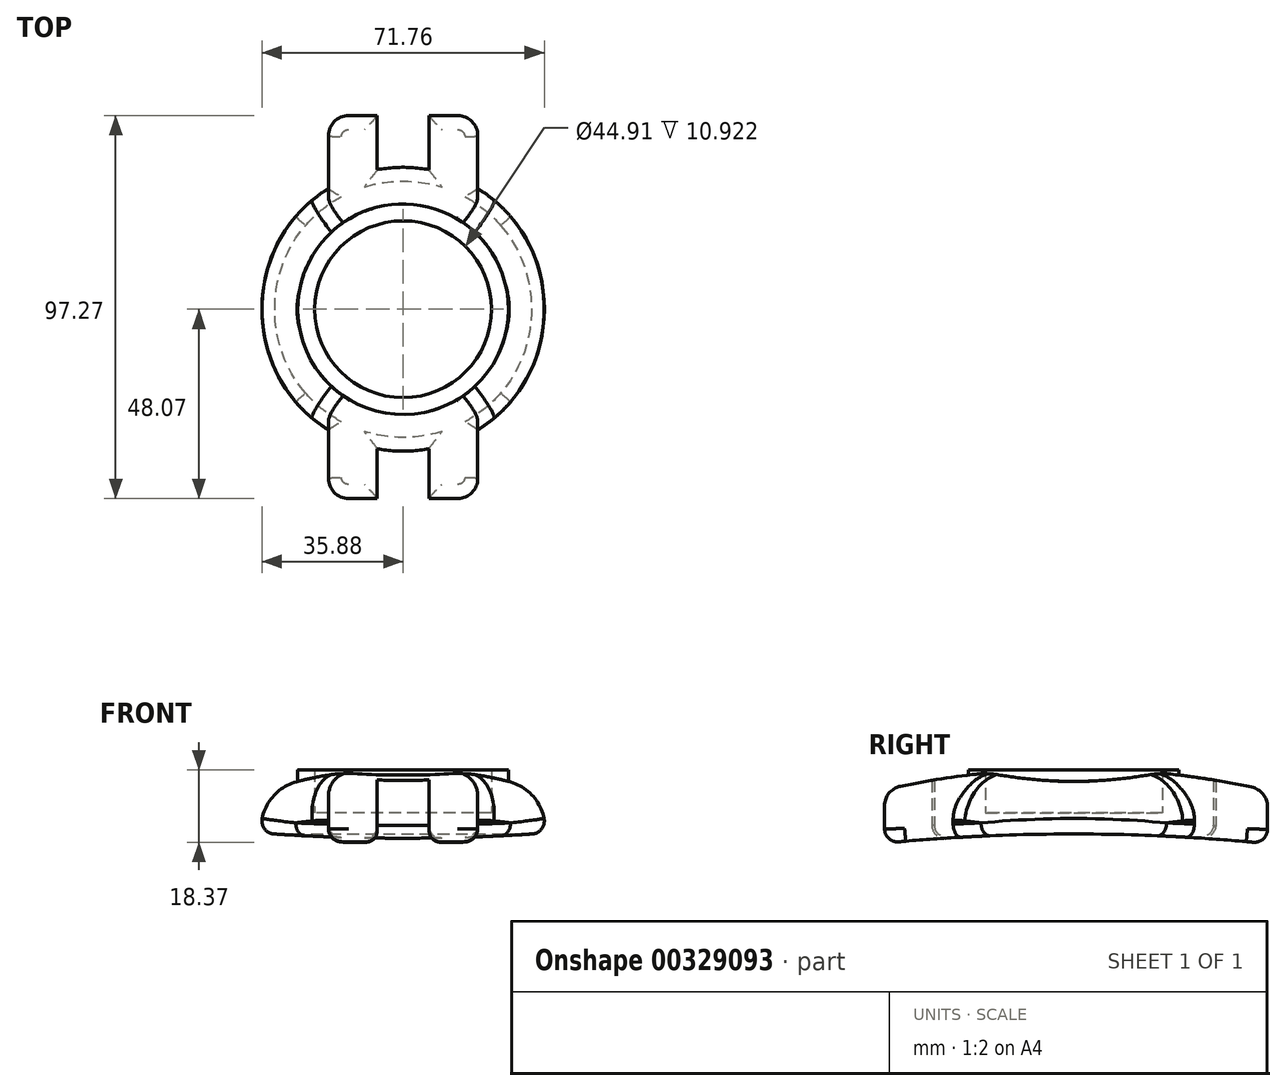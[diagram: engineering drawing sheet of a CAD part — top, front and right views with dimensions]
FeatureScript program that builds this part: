
annotation { "Feature Type Name" : "Feature", "Feature Type Description" : "" }
export const myFeature = defineFeature(function(context is Context, id is Id, definition is map)
    precondition{}
    {
        {
            var Q0;
            Q0=qCreatedBy(makeId("Top.planeOp"),FACE);
            var sketch = newSketch(context, id + "F0", { "sketchPlane" : qUnion([Q0])});
            skLineSegment(sketch, "E0.bottom", {"start": v(42.25, -55.2) * mm, "end": v(-42.25, -55.2) * mm});
            skLineSegment(sketch, "E0.top", {"start": v(42.25, 55.2) * mm, "end": v(-42.25, 55.2) * mm});
            skLineSegment(sketch, "E0.left", {"start": v(42.25, -55.2) * mm, "end": v(42.25, 55.2) * mm});
            skLineSegment(sketch, "E0.right", {"start": v(-42.25, -55.2) * mm, "end": v(-42.25, 55.2) * mm});
            skPoint(sketch, "E0.middle", {"position": v(0, 0) * mm});
            skSolve(sketch);
        }
        {
            var Q0;
            Q0=makeQuery(id+"F0.imprint","IMPRINT",FACE,{"disambiguationData":[TD([[makeQuery(id+"F0.imprint","IMPRINT",EDGE,{"derivedFrom":sQuery(id+"F0.wireOp",EDGE,"E0.bottom")}),-1.0]])]});
            extrude(context, id + "F1", {"entities" : qUnion([Q0]), "depth" : 25.4 * mm});
        }
        {
            var Q0;
            Q0=qCreatedBy(makeId("Top.planeOp"),FACE);
            var sketch = newSketch(context, id + "F2", { "sketchPlane" : qUnion([Q0])});
            skCircle(sketch, "E1", {"center": v(0, 0) * mm, "radius": 36.06 * mm});
            skLineSegment(sketch, "E2.bottom", {"start": v(-18.97, 49.2) * mm, "end": v(-6.57, 49.2) * mm});
            skLineSegment(sketch, "E2.top", {"start": v(-18.97, -48.07) * mm, "end": v(-6.57, -48.07) * mm});
            skLineSegment(sketch, "E2.left", {"start": v(-18.97, 49.2) * mm, "end": v(-18.97, -48.07) * mm});
            skLineSegment(sketch, "E2.right", {"start": v(-6.57, 49.2) * mm, "end": v(-6.57, -48.07) * mm});
            skLineSegment(sketch, "E3", {"start": v(-18.97, 0) * mm, "end": v(-6.57, 0) * mm, "construction": true});
            skLineSegment(sketch, "E4", {"start": v(0, 36.06) * mm, "end": v(0, -36.06) * mm, "construction": true});
            skLineSegment(sketch, "E5.MirrorCS", {"start": v(18.97, -48.07) * mm, "end": v(6.57, -48.07) * mm});
            skLineSegment(sketch, "E6.MirrorCS", {"start": v(6.57, 49.2) * mm, "end": v(6.57, -48.07) * mm});
            skLineSegment(sketch, "E7.MirrorCS", {"start": v(18.97, 49.2) * mm, "end": v(6.57, 49.2) * mm});
            skLineSegment(sketch, "E8.MirrorCS", {"start": v(18.97, 49.2) * mm, "end": v(18.97, -48.07) * mm});
            skLineSegment(sketch, "E9.bottom", {"start": v(47.89, 60.84) * mm, "end": v(-47.89, 60.84) * mm});
            skLineSegment(sketch, "E9.top", {"start": v(47.89, -60.84) * mm, "end": v(-47.89, -60.84) * mm});
            skLineSegment(sketch, "E9.left", {"start": v(47.89, 60.84) * mm, "end": v(47.89, -60.84) * mm});
            skLineSegment(sketch, "E9.right", {"start": v(-47.89, 60.84) * mm, "end": v(-47.89, -60.84) * mm});
            skSolve(sketch);
        }
        {
            var Q0;
            Q0 = qSketchRegion(id + "F2", true);
            extrude(context, id + "F3", {"entities" : qUnion([Q0]), "operationType" : NewBodyOperationType.REMOVE, "depth" : 84.33 * mm});
        }
        {
            var Q0;
            Q0=qCreatedBy(makeId("Front.planeOp"),FACE);
            var sketch = newSketch(context, id + "F4", { "sketchPlane" : qUnion([Q0])});
            skLineSegment(sketch, "E10.bottom", {"start": v(45.26, 29.3) * mm, "end": v(-45.26, 29.3) * mm});
            skLineSegment(sketch, "E10.top", {"start": v(45.26, -29.3) * mm, "end": v(-45.26, -29.3) * mm});
            skLineSegment(sketch, "E10.left", {"start": v(45.26, 29.3) * mm, "end": v(45.26, -29.3) * mm});
            skLineSegment(sketch, "E10.right", {"start": v(-45.26, 29.3) * mm, "end": v(-45.26, -29.3) * mm});
            skPoint(sketch, "E10.middle", {"position": v(0, 0) * mm});
            skLineSegment(sketch, "E11", {"start": v(-45.26, 10.52) * mm, "end": v(45.26, 10.52) * mm, "construction": true});
            skArc(sketch, "E12", {"start": v(45.26, 10.52) * mm, "mid": v(0, 20.57) * mm, "end": v(-45.26, 10.52) * mm});
            skSolve(sketch);
        }
        {
            var Q0;
            {var subQ0=sQuery(id+"F4.wireOp",EDGE,"E10.bottom");Q0=makeQuery(id+"F4.imprint","IMPRINT",FACE,{"disambiguationData":[TD([[makeQuery(id+"F4.imprint","IMPRINT",EDGE,{"derivedFrom":subQ0}),1.0]])]});}
            extrude(context, id + "F5", {"entities" : qUnion([Q0]), "operationType" : NewBodyOperationType.REMOVE, "oppositeDirection" : true, "depth" : 84.84 * mm});
        }
        {
            var Q0;
            Q0=makeQuery(id+"F5.boolean.opBoolean","COPY",FACE,{"derivedFrom":makeQuery(id+"F5.opExtrude","CAP_FACE",FACE,{"disambiguationData":[OSD([sQuery(id+"F4.wireOp",EDGE,"E10.bottom"),sQuery(id+"F4.wireOp",EDGE,"E10.left"),sQuery(id+"F4.wireOp",EDGE,"E10.right"),sQuery(id+"F4.wireOp",EDGE,"E12")])],"isStart":true})});
            extrude(context, id + "F6", {"entities" : qUnion([Q0]), "operationType" : NewBodyOperationType.REMOVE, "oppositeDirection" : true, "depth" : 78.74 * mm});
        }
        {
            var Q0;
            Q0=qCreatedBy(makeId("Right.planeOp"),FACE);
            var sketch = newSketch(context, id + "F7", { "sketchPlane" : qUnion([Q0])});
            skLineSegment(sketch, "E13.bottom", {"start": v(-61.4, 24.41) * mm, "end": v(61.4, 24.41) * mm});
            skLineSegment(sketch, "E13.top", {"start": v(-61.4, -24.41) * mm, "end": v(61.4, -24.41) * mm});
            skLineSegment(sketch, "E13.left", {"start": v(-61.4, 24.41) * mm, "end": v(-61.4, -24.41) * mm});
            skLineSegment(sketch, "E13.right", {"start": v(61.4, 24.41) * mm, "end": v(61.4, -24.41) * mm});
            skPoint(sketch, "E13.middle", {"position": v(0, 0) * mm});
            skArc(sketch, "E14", {"start": v(61.4, 0) * mm, "mid": v(0, 3.82) * mm, "end": v(-61.4, 0) * mm});
            skLineSegment(sketch, "E15", {"start": v(61.4, 11.64) * mm, "end": v(-61.4, 11.64) * mm, "construction": true});
            skArc(sketch, "E16", {"start": v(61.4, 11.64) * mm, "mid": v(0, 20.42) * mm, "end": v(-61.4, 11.64) * mm});
            skSolve(sketch);
        }
        {
            var Q0;
            {var subQ0=sQuery(id+"F7.wireOp",EDGE,"E13.bottom");Q0=makeQuery(id+"F7.imprint","IMPRINT",FACE,{"disambiguationData":[TD([[makeQuery(id+"F7.imprint","IMPRINT",EDGE,{"derivedFrom":subQ0}),-1.0]])]});}
            extrude(context, id + "F8", {"entities" : qUnion([Q0]), "operationType" : NewBodyOperationType.REMOVE, "oppositeDirection" : true, "depth" : 54.36 * mm});
        }
        {
            var Q0;
            {var subQ0=sQuery(id+"F7.wireOp",EDGE,"E13.bottom");Q0=makeQuery(id+"F7.imprint","IMPRINT",FACE,{"disambiguationData":[TD([[makeQuery(id+"F7.imprint","IMPRINT",EDGE,{"derivedFrom":subQ0}),-1.0]])]});}
            extrude(context, id + "F9", {"entities" : qUnion([Q0]), "operationType" : NewBodyOperationType.REMOVE, "depth" : 53.85 * mm});
        }
        {
            var Q0;
            {var subQ0=sQuery(id+"F4.wireOp",EDGE,"E12");Q0=makeQuery(id+"F8.boolean.opBoolean","INTERSECT",EDGE,{"derivedFrom":[makeQuery(id+"F6.boolean.opBoolean","MERGE",FACE,{"derivedFrom":[makeQuery(id+"F5.boolean.opBoolean","COPY",FACE,{"derivedFrom":makeQuery(id+"F5.opExtrude","SWEPT_FACE",FACE,{"disambiguationData":[OSD([subQ0])]})}),makeQuery(id+"F6.opExtrude","SWEPT_FACE",FACE,{"disambiguationData":[OSD([subQ0])]})]}),makeQuery(id+"F8.opExtrude","SWEPT_FACE",FACE,{"disambiguationData":[OSD([sQuery(id+"F7.wireOp",EDGE,"E16")])]})]});}
            var Q1;
            {var subQ0=sQuery(id+"F7.wireOp",EDGE,"E16");var subQ9=sQuery(id+"F2.wireOp",EDGE,"E5.MirrorCS");var subQ11=sQuery(id+"F4.wireOp",EDGE,"E12");Q1=makeQuery(id+"F9.boolean.opBoolean","INTERSECT",EDGE,{"derivedFrom":[makeQuery(id+"F8.boolean.opBoolean","SPLIT",FACE,{"disambiguationData":[TD([makeQuery(id+"F3.boolean.opBoolean","COPY",FACE,{"derivedFrom":makeQuery(id+"F3.opExtrude","SWEPT_FACE",FACE,{"disambiguationData":[OSD([subQ9])]})})])],"derivedFrom":makeQuery(id+"F6.boolean.opBoolean","MERGE",FACE,{"derivedFrom":[makeQuery(id+"F5.boolean.opBoolean","COPY",FACE,{"derivedFrom":makeQuery(id+"F5.opExtrude","SWEPT_FACE",FACE,{"disambiguationData":[OSD([subQ11])]})}),makeQuery(id+"F6.opExtrude","SWEPT_FACE",FACE,{"disambiguationData":[OSD([subQ11])]})]})}),makeQuery(id+"F9.opExtrude","SWEPT_FACE",FACE,{"disambiguationData":[OSD([subQ0])]})]});}
            fillet(context, id + "F10", {"entities" : qUnion([Q0, Q1]), "radius" : 27.7 * mm, "tangentPropagation" : true, "allowEdgeOverflow" : false});
        }
        {
            var Q0;
            {var subQ0=sQuery(id+"F2.wireOp",EDGE,"E8.MirrorCS");Q0=makeQuery(id+"F9.boolean.opBoolean","INTERSECT",EDGE,{"derivedFrom":[makeQuery(id+"F3.boolean.opBoolean","COPY",FACE,{"derivedFrom":makeQuery(id+"F3.opExtrude","SWEPT_FACE",FACE,{"disambiguationData":[OSD([subQ0]),TDD([makeQuery(id+"F2.imprint","IMPRINT",EDGE,{"disambiguationData":[TD([[makeQuery(id+"F2.imprint","INTERSECT",VERTEX,{"derivedFrom":[sQuery(id+"F2.wireOp",EDGE,"E7.MirrorCS"),subQ0]}),-1.0]])],"derivedFrom":subQ0})])]})}),makeQuery(id+"F9.opExtrude","SWEPT_FACE",FACE,{"disambiguationData":[OSD([sQuery(id+"F7.wireOp",EDGE,"E16")])]})]});}
            var Q1;
            Q1=makeQuery(id+"F3.boolean.opBoolean","COPY",EDGE,{"derivedFrom":makeQuery(id+"F3.opExtrude","SWEPT_EDGE",EDGE,{"disambiguationData":[OSD([sQuery(id+"F2.wireOp",EDGE,"E7.MirrorCS"),sQuery(id+"F2.wireOp",EDGE,"E8.MirrorCS")])]})});
            var Q2;
            {var subQ0=sQuery(id+"F2.wireOp",EDGE,"E8.MirrorCS");Q2=makeQuery(id+"F9.boolean.opBoolean","INTERSECT",EDGE,{"derivedFrom":[makeQuery(id+"F3.boolean.opBoolean","COPY",FACE,{"derivedFrom":makeQuery(id+"F3.opExtrude","SWEPT_FACE",FACE,{"disambiguationData":[OSD([subQ0]),TDD([makeQuery(id+"F2.imprint","IMPRINT",EDGE,{"disambiguationData":[TD([[makeQuery(id+"F2.imprint","INTERSECT",VERTEX,{"derivedFrom":[sQuery(id+"F2.wireOp",EDGE,"E5.MirrorCS"),subQ0]}),1.0]])],"derivedFrom":subQ0})])]})}),makeQuery(id+"F9.opExtrude","SWEPT_FACE",FACE,{"disambiguationData":[OSD([sQuery(id+"F7.wireOp",EDGE,"E16")])]})]});}
            var Q3;
            Q3=makeQuery(id+"F3.boolean.opBoolean","COPY",EDGE,{"derivedFrom":makeQuery(id+"F3.opExtrude","SWEPT_EDGE",EDGE,{"disambiguationData":[OSD([sQuery(id+"F2.wireOp",EDGE,"E5.MirrorCS"),sQuery(id+"F2.wireOp",EDGE,"E8.MirrorCS")])]})});
            var Q4;
            Q4=makeQuery(id+"F9.boolean.opBoolean","INTERSECT",EDGE,{"derivedFrom":[makeQuery(id+"F3.boolean.opBoolean","COPY",FACE,{"derivedFrom":makeQuery(id+"F3.opExtrude","SWEPT_FACE",FACE,{"disambiguationData":[OSD([sQuery(id+"F2.wireOp",EDGE,"E5.MirrorCS")])]})}),makeQuery(id+"F9.opExtrude","SWEPT_FACE",FACE,{"disambiguationData":[OSD([sQuery(id+"F7.wireOp",EDGE,"E16")])]})]});
            var Q5;
            Q5=makeQuery(id+"F9.boolean.opBoolean","INTERSECT",EDGE,{"derivedFrom":[makeQuery(id+"F3.boolean.opBoolean","COPY",FACE,{"derivedFrom":makeQuery(id+"F3.opExtrude","SWEPT_FACE",FACE,{"disambiguationData":[OSD([sQuery(id+"F2.wireOp",EDGE,"E7.MirrorCS")])]})}),makeQuery(id+"F9.opExtrude","SWEPT_FACE",FACE,{"disambiguationData":[OSD([sQuery(id+"F7.wireOp",EDGE,"E16")])]})]});
            var Q6;
            Q6=makeQuery(id+"F3.boolean.opBoolean","COPY",EDGE,{"derivedFrom":makeQuery(id+"F3.opExtrude","SWEPT_EDGE",EDGE,{"disambiguationData":[OSD([sQuery(id+"F2.wireOp",EDGE,"E2.top"),sQuery(id+"F2.wireOp",EDGE,"E2.left")])]})});
            var Q7;
            {var subQ0=sQuery(id+"F2.wireOp",EDGE,"E2.left");Q7=makeQuery(id+"F8.boolean.opBoolean","INTERSECT",EDGE,{"derivedFrom":[makeQuery(id+"F3.boolean.opBoolean","COPY",FACE,{"derivedFrom":makeQuery(id+"F3.opExtrude","SWEPT_FACE",FACE,{"disambiguationData":[OSD([subQ0]),TDD([makeQuery(id+"F2.imprint","IMPRINT",EDGE,{"disambiguationData":[TD([[makeQuery(id+"F2.imprint","INTERSECT",VERTEX,{"derivedFrom":[sQuery(id+"F2.wireOp",EDGE,"E2.top"),subQ0]}),1.0]])],"derivedFrom":subQ0})])]})}),makeQuery(id+"F8.opExtrude","SWEPT_FACE",FACE,{"disambiguationData":[OSD([sQuery(id+"F7.wireOp",EDGE,"E16")])]})]});}
            var Q8;
            {var subQ0=sQuery(id+"F2.wireOp",EDGE,"E2.left");Q8=makeQuery(id+"F8.boolean.opBoolean","INTERSECT",EDGE,{"derivedFrom":[makeQuery(id+"F3.boolean.opBoolean","COPY",FACE,{"derivedFrom":makeQuery(id+"F3.opExtrude","SWEPT_FACE",FACE,{"disambiguationData":[OSD([subQ0]),TDD([makeQuery(id+"F2.imprint","IMPRINT",EDGE,{"disambiguationData":[TD([[makeQuery(id+"F2.imprint","INTERSECT",VERTEX,{"derivedFrom":[sQuery(id+"F2.wireOp",EDGE,"E2.bottom"),subQ0]}),-1.0]])],"derivedFrom":subQ0})])]})}),makeQuery(id+"F8.opExtrude","SWEPT_FACE",FACE,{"disambiguationData":[OSD([sQuery(id+"F7.wireOp",EDGE,"E16")])]})]});}
            var Q9;
            Q9=makeQuery(id+"F8.boolean.opBoolean","INTERSECT",EDGE,{"derivedFrom":[makeQuery(id+"F3.boolean.opBoolean","COPY",FACE,{"derivedFrom":makeQuery(id+"F3.opExtrude","SWEPT_FACE",FACE,{"disambiguationData":[OSD([sQuery(id+"F2.wireOp",EDGE,"E2.top")])]})}),makeQuery(id+"F8.opExtrude","SWEPT_FACE",FACE,{"disambiguationData":[OSD([sQuery(id+"F7.wireOp",EDGE,"E16")])]})]});
            var Q10;
            Q10=makeQuery(id+"F8.boolean.opBoolean","INTERSECT",EDGE,{"derivedFrom":[makeQuery(id+"F3.boolean.opBoolean","COPY",FACE,{"derivedFrom":makeQuery(id+"F3.opExtrude","SWEPT_FACE",FACE,{"disambiguationData":[OSD([sQuery(id+"F2.wireOp",EDGE,"E2.bottom")])]})}),makeQuery(id+"F8.opExtrude","SWEPT_FACE",FACE,{"disambiguationData":[OSD([sQuery(id+"F7.wireOp",EDGE,"E16")])]})]});
            var Q11;
            Q11=makeQuery(id+"F3.boolean.opBoolean","COPY",EDGE,{"derivedFrom":makeQuery(id+"F3.opExtrude","SWEPT_EDGE",EDGE,{"disambiguationData":[OSD([sQuery(id+"F2.wireOp",EDGE,"E2.bottom"),sQuery(id+"F2.wireOp",EDGE,"E2.left")])]})});
            fillet(context, id + "F11", {"entities" : qUnion([Q0, Q1, Q2, Q3, Q4, Q5, Q6, Q7, Q8, Q9, Q10, Q11]), "radius" : 5.08 * mm, "tangentPropagation" : true, "allowEdgeOverflow" : false});
        }
        {
            var Q0;
            {var subQ0=sQuery(id+"F2.wireOp",EDGE,"E8.MirrorCS");var subQ1=sQuery(id+"F2.wireOp",EDGE,"E1");Q0=makeQuery(id+"F6.boolean.opBoolean","INTERSECT",EDGE,{"derivedFrom":[makeQuery(id+"F3.boolean.opBoolean","COPY",FACE,{"derivedFrom":makeQuery(id+"F3.opExtrude","SWEPT_FACE",FACE,{"disambiguationData":[OSD([subQ1]),TDD([makeQuery(id+"F2.imprint","IMPRINT",EDGE,{"disambiguationData":[TD([[makeQuery(id+"F2.imprint","INTERSECT",VERTEX,{"disambiguationData":[OD(0.0)],"derivedFrom":[subQ1,subQ0]}),1.0]])],"derivedFrom":subQ1})])]})}),makeQuery(id+"F6.opExtrude","SWEPT_FACE",FACE,{"disambiguationData":[OSD([sQuery(id+"F4.wireOp",EDGE,"E12")])]})]});}
            var Q1;
            {var subQ0=sQuery(id+"F2.wireOp",EDGE,"E8.MirrorCS");var subQ1=sQuery(id+"F2.wireOp",EDGE,"E1");var subQ2=makeQuery(id+"F2.imprint","INTERSECT",VERTEX,{"disambiguationData":[OD(0.0)],"derivedFrom":[subQ1,subQ0]});var subQ4=makeQuery(id+"F3.boolean.opBoolean","COPY",FACE,{"derivedFrom":makeQuery(id+"F3.opExtrude","SWEPT_FACE",FACE,{"disambiguationData":[OSD([subQ1]),TDD([makeQuery(id+"F2.imprint","IMPRINT",EDGE,{"disambiguationData":[TD([[subQ2,1.0]])],"derivedFrom":subQ1})])]})});var subQ5=sQuery(id+"F7.wireOp",EDGE,"E16");var subQ10=sQuery(id+"F2.wireOp",EDGE,"E5.MirrorCS");var subQ12=sQuery(id+"F4.wireOp",EDGE,"E12");Q1=makeQuery(id+"F10.opFillet","BLEND_EDGE",EDGE,{"disambiguationData":[OD(1.0)],"blendedFrom":[makeQuery(id+"F9.boolean.opBoolean","INTERSECT",EDGE,{"derivedFrom":[makeQuery(id+"F8.boolean.opBoolean","SPLIT",FACE,{"disambiguationData":[TD([makeQuery(id+"F3.boolean.opBoolean","COPY",FACE,{"derivedFrom":makeQuery(id+"F3.opExtrude","SWEPT_FACE",FACE,{"disambiguationData":[OSD([subQ10])]})})])],"derivedFrom":makeQuery(id+"F6.boolean.opBoolean","MERGE",FACE,{"derivedFrom":[makeQuery(id+"F5.boolean.opBoolean","COPY",FACE,{"derivedFrom":makeQuery(id+"F5.opExtrude","SWEPT_FACE",FACE,{"disambiguationData":[OSD([subQ12])]})}),makeQuery(id+"F6.opExtrude","SWEPT_FACE",FACE,{"disambiguationData":[OSD([subQ12])]})]})}),makeQuery(id+"F9.opExtrude","SWEPT_FACE",FACE,{"disambiguationData":[OSD([subQ5])]})]}),subQ4],"blendedInto":[subQ4]});}
            var Q2;
            {var subQ0=sQuery(id+"F2.wireOp",EDGE,"E8.MirrorCS");var subQ1=sQuery(id+"F2.wireOp",EDGE,"E1");var subQ2=makeQuery(id+"F2.imprint","INTERSECT",VERTEX,{"disambiguationData":[OD(0.0)],"derivedFrom":[subQ1,subQ0]});var subQ4=makeQuery(id+"F3.boolean.opBoolean","COPY",FACE,{"derivedFrom":makeQuery(id+"F3.opExtrude","SWEPT_FACE",FACE,{"disambiguationData":[OSD([subQ1]),TDD([makeQuery(id+"F2.imprint","IMPRINT",EDGE,{"disambiguationData":[TD([[subQ2,1.0]])],"derivedFrom":subQ1})])]})});var subQ5=sQuery(id+"F7.wireOp",EDGE,"E16");var subQ10=sQuery(id+"F2.wireOp",EDGE,"E5.MirrorCS");var subQ12=sQuery(id+"F4.wireOp",EDGE,"E12");Q2=makeQuery(id+"F10.opFillet","BLEND_EDGE",EDGE,{"disambiguationData":[OD(0.0)],"blendedFrom":[makeQuery(id+"F9.boolean.opBoolean","INTERSECT",EDGE,{"derivedFrom":[makeQuery(id+"F8.boolean.opBoolean","SPLIT",FACE,{"disambiguationData":[TD([makeQuery(id+"F3.boolean.opBoolean","COPY",FACE,{"derivedFrom":makeQuery(id+"F3.opExtrude","SWEPT_FACE",FACE,{"disambiguationData":[OSD([subQ10])]})})])],"derivedFrom":makeQuery(id+"F6.boolean.opBoolean","MERGE",FACE,{"derivedFrom":[makeQuery(id+"F5.boolean.opBoolean","COPY",FACE,{"derivedFrom":makeQuery(id+"F5.opExtrude","SWEPT_FACE",FACE,{"disambiguationData":[OSD([subQ12])]})}),makeQuery(id+"F6.opExtrude","SWEPT_FACE",FACE,{"disambiguationData":[OSD([subQ12])]})]})}),makeQuery(id+"F9.opExtrude","SWEPT_FACE",FACE,{"disambiguationData":[OSD([subQ5])]})]}),subQ4],"blendedInto":[subQ4]});}
            var Q3;
            {var subQ0=sQuery(id+"F2.wireOp",EDGE,"E2.left");var subQ1=sQuery(id+"F2.wireOp",EDGE,"E1");Q3=makeQuery(id+"F6.boolean.opBoolean","INTERSECT",EDGE,{"derivedFrom":[makeQuery(id+"F3.boolean.opBoolean","COPY",FACE,{"derivedFrom":makeQuery(id+"F3.opExtrude","SWEPT_FACE",FACE,{"disambiguationData":[OSD([subQ1]),TDD([makeQuery(id+"F2.imprint","IMPRINT",EDGE,{"disambiguationData":[TD([[makeQuery(id+"F2.imprint","INTERSECT",VERTEX,{"disambiguationData":[OD(0.0)],"derivedFrom":[subQ1,subQ0]}),-1.0]])],"derivedFrom":subQ1})])]})}),makeQuery(id+"F6.opExtrude","SWEPT_FACE",FACE,{"disambiguationData":[OSD([sQuery(id+"F4.wireOp",EDGE,"E12")])]})]});}
            var Q4;
            {var subQ0=sQuery(id+"F2.wireOp",EDGE,"E2.left");var subQ1=sQuery(id+"F2.wireOp",EDGE,"E1");var subQ2=sQuery(id+"F4.wireOp",EDGE,"E12");Q4=makeQuery(id+"F10.opFillet","BLEND_EDGE",EDGE,{"disambiguationData":[OD(0.0)],"blendedFrom":[makeQuery(id+"F8.boolean.opBoolean","INTERSECT",EDGE,{"derivedFrom":[makeQuery(id+"F6.boolean.opBoolean","MERGE",FACE,{"derivedFrom":[makeQuery(id+"F5.boolean.opBoolean","COPY",FACE,{"derivedFrom":makeQuery(id+"F5.opExtrude","SWEPT_FACE",FACE,{"disambiguationData":[OSD([subQ2])]})}),makeQuery(id+"F6.opExtrude","SWEPT_FACE",FACE,{"disambiguationData":[OSD([subQ2])]})]}),makeQuery(id+"F8.opExtrude","SWEPT_FACE",FACE,{"disambiguationData":[OSD([sQuery(id+"F7.wireOp",EDGE,"E16")])]})]}),makeQuery(id+"F3.boolean.opBoolean","COPY",FACE,{"derivedFrom":makeQuery(id+"F3.opExtrude","SWEPT_FACE",FACE,{"disambiguationData":[OSD([subQ1]),TDD([makeQuery(id+"F2.imprint","IMPRINT",EDGE,{"disambiguationData":[TD([[makeQuery(id+"F2.imprint","INTERSECT",VERTEX,{"disambiguationData":[OD(0.0)],"derivedFrom":[subQ1,subQ0]}),-1.0]])],"derivedFrom":subQ1})])]})})],"blendedInto":[makeQuery(id+"F3.boolean.opBoolean","COPY",FACE,{"derivedFrom":makeQuery(id+"F3.opExtrude","SWEPT_FACE",FACE,{"disambiguationData":[OSD([subQ1]),TDD([makeQuery(id+"F2.imprint","IMPRINT",EDGE,{"disambiguationData":[TD([[makeQuery(id+"F2.imprint","INTERSECT",VERTEX,{"disambiguationData":[OD(0.0)],"derivedFrom":[subQ1,subQ0]}),-1.0]])],"derivedFrom":subQ1})])]})})]});}
            var Q5;
            {var subQ0=sQuery(id+"F2.wireOp",EDGE,"E2.left");var subQ1=sQuery(id+"F2.wireOp",EDGE,"E1");var subQ2=sQuery(id+"F4.wireOp",EDGE,"E12");Q5=makeQuery(id+"F10.opFillet","BLEND_EDGE",EDGE,{"disambiguationData":[OD(1.0)],"blendedFrom":[makeQuery(id+"F8.boolean.opBoolean","INTERSECT",EDGE,{"derivedFrom":[makeQuery(id+"F6.boolean.opBoolean","MERGE",FACE,{"derivedFrom":[makeQuery(id+"F5.boolean.opBoolean","COPY",FACE,{"derivedFrom":makeQuery(id+"F5.opExtrude","SWEPT_FACE",FACE,{"disambiguationData":[OSD([subQ2])]})}),makeQuery(id+"F6.opExtrude","SWEPT_FACE",FACE,{"disambiguationData":[OSD([subQ2])]})]}),makeQuery(id+"F8.opExtrude","SWEPT_FACE",FACE,{"disambiguationData":[OSD([sQuery(id+"F7.wireOp",EDGE,"E16")])]})]}),makeQuery(id+"F3.boolean.opBoolean","COPY",FACE,{"derivedFrom":makeQuery(id+"F3.opExtrude","SWEPT_FACE",FACE,{"disambiguationData":[OSD([subQ1]),TDD([makeQuery(id+"F2.imprint","IMPRINT",EDGE,{"disambiguationData":[TD([[makeQuery(id+"F2.imprint","INTERSECT",VERTEX,{"disambiguationData":[OD(0.0)],"derivedFrom":[subQ1,subQ0]}),-1.0]])],"derivedFrom":subQ1})])]})})],"blendedInto":[makeQuery(id+"F3.boolean.opBoolean","COPY",FACE,{"derivedFrom":makeQuery(id+"F3.opExtrude","SWEPT_FACE",FACE,{"disambiguationData":[OSD([subQ1]),TDD([makeQuery(id+"F2.imprint","IMPRINT",EDGE,{"disambiguationData":[TD([[makeQuery(id+"F2.imprint","INTERSECT",VERTEX,{"disambiguationData":[OD(0.0)],"derivedFrom":[subQ1,subQ0]}),-1.0]])],"derivedFrom":subQ1})])]})})]});}
            fillet(context, id + "F12", {"entities" : qUnion([Q0, Q1, Q2, Q3, Q4, Q5]), "radius" : 12.2 * mm, "tangentPropagation" : true, "allowEdgeOverflow" : false});
        }
        {
            var Q0;
            {var subQ0=sQuery(id+"F7.wireOp",EDGE,"E13.top");Q0=makeQuery(id+"F7.imprint","IMPRINT",FACE,{"disambiguationData":[TD([[makeQuery(id+"F7.imprint","IMPRINT",EDGE,{"derivedFrom":subQ0}),1.0]])]});}
            extrude(context, id + "F13", {"entities" : qUnion([Q0]), "operationType" : NewBodyOperationType.REMOVE, "oppositeDirection" : true, "depth" : 63.25 * mm});
        }
        {
            var Q0;
            {var subQ0=sQuery(id+"F7.wireOp",EDGE,"E13.top");Q0=makeQuery(id+"F7.imprint","IMPRINT",FACE,{"disambiguationData":[TD([[makeQuery(id+"F7.imprint","IMPRINT",EDGE,{"derivedFrom":subQ0}),1.0]])]});}
            extrude(context, id + "F14", {"entities" : qUnion([Q0]), "operationType" : NewBodyOperationType.REMOVE, "depth" : 39.12 * mm});
        }
        {
            var Q0;
            {var subQ0=sQuery(id+"F7.wireOp",EDGE,"E14");Q0=makeQuery(id+"F14.boolean.opBoolean","MERGE",FACE,{"derivedFrom":[makeQuery(id+"F13.boolean.opBoolean","COPY",FACE,{"derivedFrom":makeQuery(id+"F13.opExtrude","SWEPT_FACE",FACE,{"disambiguationData":[OSD([subQ0])]})}),makeQuery(id+"F14.opExtrude","SWEPT_FACE",FACE,{"disambiguationData":[OSD([subQ0])]})]});}
            fillet(context, id + "F15", {"entities" : qUnion([Q0]), "radius" : 3.28 * mm, "tangentPropagation" : true, "allowEdgeOverflow" : false});
        }
        {
            var Q0;
            Q0=qCreatedBy(makeId("Top.planeOp"),FACE);
            cPlane(context, id + "F16", {"entities" : qUnion([Q0]), "cplaneType" : CPlaneType.OFFSET, "offset" : 9.14 * mm, "width" : 152.4 * mm, "height" : 152.4 * mm});
        }
        {
            var Q0;
            Q0=qCreatedBy(id+"F16.planeOp",FACE);
            var sketch = newSketch(context, id + "F17", { "sketchPlane" : qUnion([Q0])});
            skCircle(sketch, "E17", {"center": v(0, 0) * mm, "radius": 26.75 * mm});
            skSolve(sketch);
        }
        {
            var Q0;
            Q0 = qSketchRegion(id + "F17", true);
            extrude(context, id + "F18", {"entities" : qUnion([Q0]), "operationType" : NewBodyOperationType.ADD, "depth" : 10.92 * mm});
        }
        {
            var Q0;
            Q0=qCreatedBy(id+"F16.planeOp",FACE);
            var sketch = newSketch(context, id + "F19", { "sketchPlane" : qUnion([Q0])});
            skCircle(sketch, "E18", {"center": v(0, 0) * mm, "radius": 22.46 * mm});
            skSolve(sketch);
        }
        {
            var Q0;
            Q0 = qSketchRegion(id + "F19", true);
            extrude(context, id + "F20", {"entities" : qUnion([Q0]), "operationType" : NewBodyOperationType.REMOVE, "depth" : 25.4 * mm});
        }
    });
